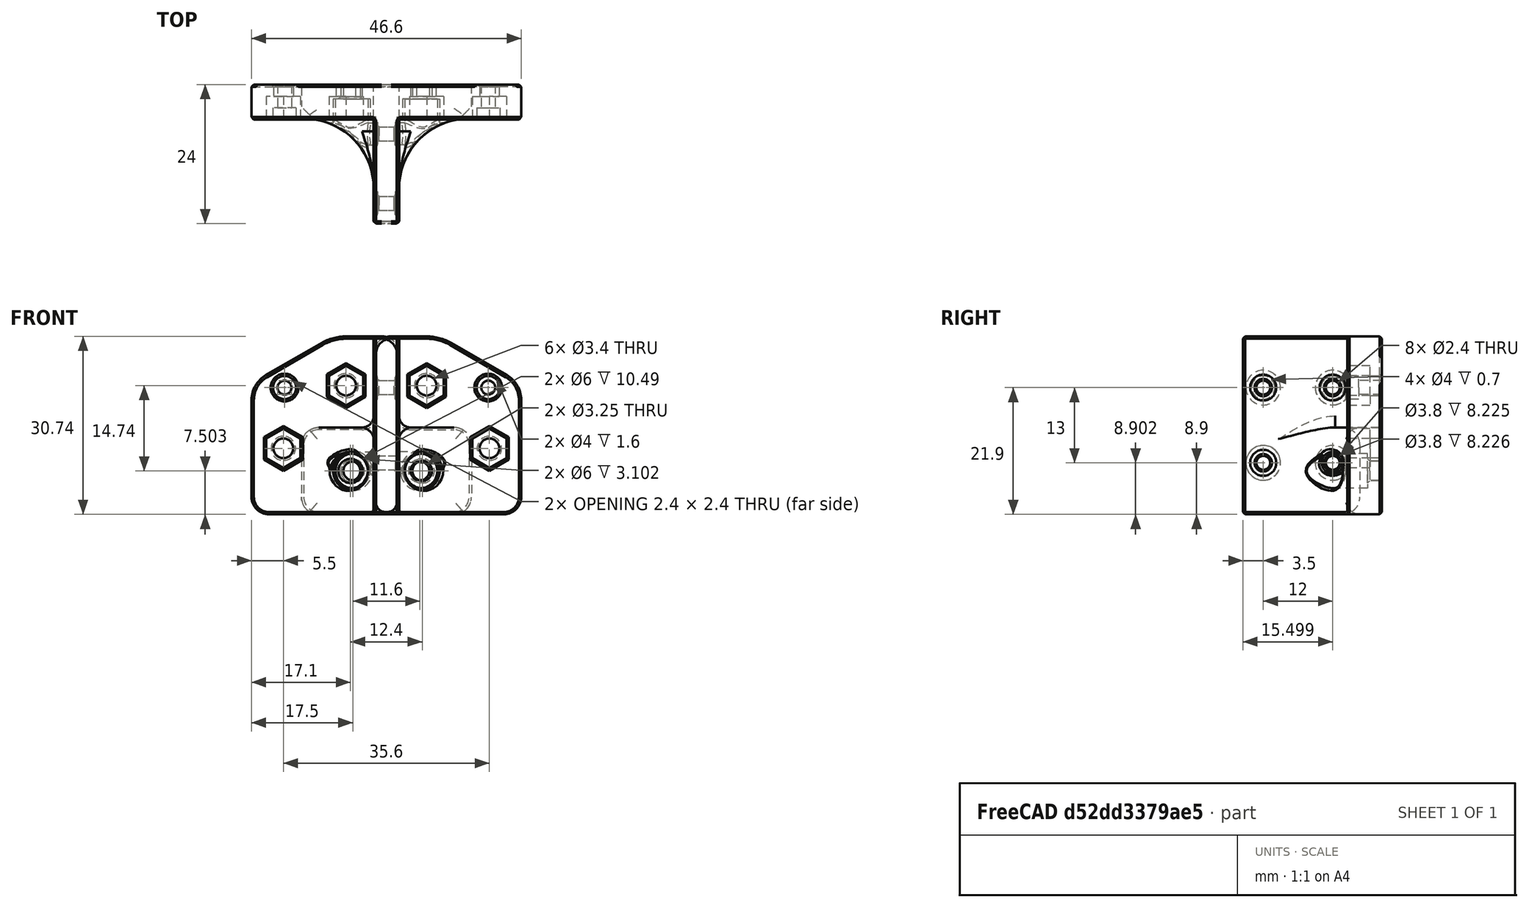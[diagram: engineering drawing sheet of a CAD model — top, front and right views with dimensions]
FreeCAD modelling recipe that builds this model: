
FCSTD DOCUMENT  (FreeCAD 0.18R16146 (Git))
Label: xy-join-btm
License: Other
LicenseURL: GPL3
objects: Part::Cylinder×20, Part::MultiFuse×8, Part::Cut×4, Part::Feature×2, Part::Chamfer×2, App::Part×1
note: 36 computed .brp shape members not serialized (recipe doc carries the construction recipe); baked Part::Feature solids carry a one-line shape summary decoded from their .brp

FEATURE [Part::Feature] Part__Feature239  label="XY_Joint_Right001"
  Placement = pos=(-46.3999,-36.3584,-1.5623) rot=(0,0,1;0rad)
  shape: bbox 38.02 x 24.02 x 30.76 mm, 140 faces (baked)
FEATURE [Part::Feature] Part__Feature148  label="XY_Joint_Left003"
  Placement = pos=(-18.9999,-36.3584,-1.5623) rot=(0,0,1;0rad)
  shape: bbox 38.02 x 24.02 x 30.76 mm, 139 faces (baked)
FEATURE [Part::Cylinder] Cylinder001
  Angle = 360
  AttacherType = Attacher::AttachEngine3D
  Height = 0.7
  Placement = pos=(-4.4,3.5,21.9) rot=(0,1,0;1.5708rad)
  Radius = 2
FEATURE [Part::Cylinder] Cylinder002
  Angle = 360
  AttacherType = Attacher::AttachEngine3D
  Height = 0.7
  Placement = pos=(-4.4,15.5,21.9) rot=(0,1,0;1.5708rad)
  Radius = 2
FEATURE [Part::Cylinder] Cylinder004
  Angle = 360
  AttacherType = Attacher::AttachEngine3D
  Height = 4
  Placement = pos=(-4.4,15.5,8.9) rot=(0,1,0;1.5708rad)
  Radius = 3
FEATURE [Part::Cylinder] Cylinder005
  Angle = 360
  AttacherType = Attacher::AttachEngine3D
  Height = 4.4
  Placement = pos=(-4.4,15.5,21.9) rot=(0,1,0;1.5708rad)
  Radius = 3
FEATURE [Part::Cylinder] Cylinder006
  Angle = 360
  AttacherType = Attacher::AttachEngine3D
  Height = 4.4
  Placement = pos=(-4.4,3.5,21.9) rot=(0,1,0;1.5708rad)
  Radius = 3
FEATURE [Part::Cylinder] Cylinder007
  Angle = 360
  AttacherType = Attacher::AttachEngine3D
  Height = 4.4
  Placement = pos=(-4.4,3.5,8.9) rot=(0,1,0;1.5708rad)
  Radius = 3
FEATURE [Part::Cylinder] Cylinder008
  Angle = 360
  AttacherType = Attacher::AttachEngine3D
  Height = 4.4
  Placement = pos=(-4.4,3.5,8.9) rot=(0,1,0;1.5708rad)
  Radius = 1.2
FEATURE [Part::Cylinder] Cylinder009
  Angle = 360
  AttacherType = Attacher::AttachEngine3D
  Height = 4.4
  Placement = pos=(-4.4,3.5,21.9) rot=(0,1,0;1.5708rad)
  Radius = 1.2
FEATURE [Part::Cylinder] Cylinder010
  Angle = 360
  AttacherType = Attacher::AttachEngine3D
  Height = 4.4
  Placement = pos=(-4.4,15.5,21.9) rot=(0,1,0;1.5708rad)
  Radius = 1.2
FEATURE [Part::Cylinder] Cylinder011
  Angle = 360
  AttacherType = Attacher::AttachEngine3D
  Height = 4
  Placement = pos=(-4.4,15.5,8.9) rot=(0,1,0;1.5708rad)
  Radius = 1.2
FEATURE [Part::MultiFuse] Fusion
  Shapes = -> [Cylinder007,Cylinder006,Cylinder005,Cylinder004]
FEATURE [Part::MultiFuse] Fusion001
  Shapes = -> [Part__Feature148,Fusion]
FEATURE [Part::MultiFuse] Fusion002
  Shapes = -> [Cylinder011,Cylinder009,Cylinder010,Cylinder008]
FEATURE [Part::Cut] Cut
  Base = -> Fusion001
  Tool = -> Fusion002
FEATURE [Part::Cylinder] Cylinder012
  Angle = 360
  AttacherType = Attacher::AttachEngine3D
  Height = 0.7
  Placement = pos=(-4.4,3.5,21.9) rot=(0,1,0;1.5708rad)
  Radius = 2
FEATURE [Part::Cylinder] Cylinder013
  Angle = 360
  AttacherType = Attacher::AttachEngine3D
  Height = 0.7
  Placement = pos=(-4.4,15.5,21.9) rot=(0,1,0;1.5708rad)
  Radius = 2
FEATURE [Part::MultiFuse] Fusion003
  Placement = pos=(3.7,0,0) rot=(0,0,1;0rad)
  Shapes = -> [Cylinder012,Cylinder013]
FEATURE [Part::Cut] Cut001
  Base = -> Cut
  Tool = -> Fusion003
FEATURE [Part::Chamfer] Chamfer
  Base = -> Cut001
  Edges = 8 edges r=0.2: [Edge190,Edge193,Edge279,Edge285,Edge299,Edge343,Edge344,Edge345]
FEATURE [App::Part] Part  label="left"
  Group = -> [Part__Feature148,Cylinder004,Cylinder005,Cylinder006,Cylinder007,Cylinder012,Cut001,Cylinder011,Fusion001,Cylinder009,Cut,Fusion,Cylinder010,Cylinder008,Fusion002,Fusion003,Cylinder013,Chamfer]
  Origin = -> Origin
FEATURE [Part::Cylinder] Cylinder014
  Angle = 360
  AttacherType = Attacher::AttachEngine3D
  Height = 4.4
  Placement = pos=(-4.4,3.5,8.9) rot=(0,1,0;1.5708rad)
  Radius = 3
FEATURE [Part::Cylinder] Cylinder015
  Angle = 360
  AttacherType = Attacher::AttachEngine3D
  Height = 4.4
  Placement = pos=(-4.4,3.5,21.9) rot=(0,1,0;1.5708rad)
  Radius = 3
FEATURE [Part::Cylinder] Cylinder016
  Angle = 360
  AttacherType = Attacher::AttachEngine3D
  Height = 4
  Placement = pos=(-4,15.5,8.9) rot=(0,1,0;1.5708rad)
  Radius = 3
FEATURE [Part::Cylinder] Cylinder017
  Angle = 360
  AttacherType = Attacher::AttachEngine3D
  Height = 4.4
  Placement = pos=(-4.4,15.5,21.9) rot=(0,1,0;1.5708rad)
  Radius = 3
FEATURE [Part::Cylinder] Cylinder018
  Angle = 360
  AttacherType = Attacher::AttachEngine3D
  Height = 4.4
  Placement = pos=(-4.4,3.5,8.9) rot=(0,1,0;1.5708rad)
  Radius = 1.2
FEATURE [Part::Cylinder] Cylinder019
  Angle = 360
  AttacherType = Attacher::AttachEngine3D
  Height = 4.4
  Placement = pos=(-4.4,3.5,21.9) rot=(0,1,0;1.5708rad)
  Radius = 1.2
FEATURE [Part::Cylinder] Cylinder020
  Angle = 360
  AttacherType = Attacher::AttachEngine3D
  Height = 4.4
  Placement = pos=(-4.4,15.5,8.9) rot=(0,1,0;1.5708rad)
  Radius = 1.2
FEATURE [Part::Cylinder] Cylinder021
  Angle = 360
  AttacherType = Attacher::AttachEngine3D
  Height = 4.4
  Placement = pos=(-4.4,15.5,21.9) rot=(0,1,0;1.5708rad)
  Radius = 1.2
FEATURE [Part::MultiFuse] Fusion006
  Shapes = -> [Cylinder021,Cylinder020,Cylinder019,Cylinder018]
FEATURE [Part::MultiFuse] Fusion007
  Shapes = -> [Cylinder014,Cylinder015,Cylinder016,Cylinder017]
FEATURE [Part::MultiFuse] Fusion008
  Shapes = -> [Part__Feature239,Fusion007]
FEATURE [Part::Cut] Cut002
  Base = -> Fusion008
  Tool = -> Fusion006
FEATURE [Part::MultiFuse] Fusion009
  Shapes = -> [Cylinder002,Cylinder001]
FEATURE [Part::Cut] Cut003
  Base = -> Cut002
  Tool = -> Fusion009
FEATURE [Part::Chamfer] Chamfer001
  Base = -> Cut003
  Edges = 8 edges r=0.2: [Edge68,Edge82,Edge99,Edge119,Edge300,Edge301,Edge354,Edge356]
